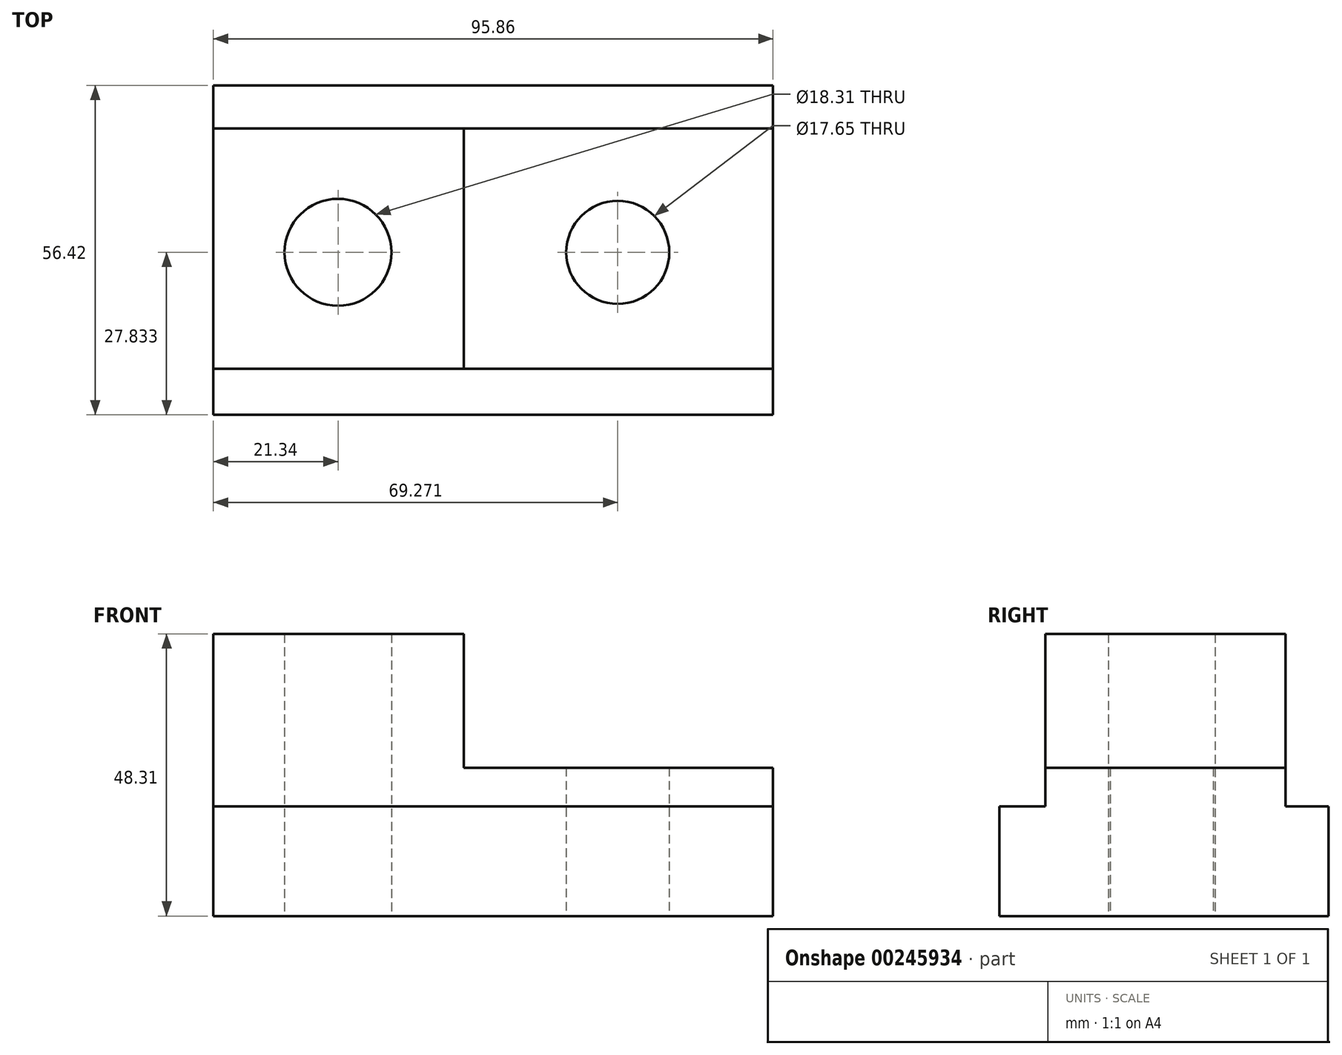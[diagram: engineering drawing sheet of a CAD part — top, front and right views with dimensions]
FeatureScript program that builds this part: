
annotation { "Feature Type Name" : "Feature", "Feature Type Description" : "" }
export const myFeature = defineFeature(function(context is Context, id is Id, definition is map)
    precondition{}
    {
        {
            var Q0;
            Q0=qCreatedBy(makeId("Top.planeOp"),FACE);
            var sketch = newSketch(context, id + "F0", { "sketchPlane" : qUnion([Q0])});
            skLineSegment(sketch, "E0.bottom", {"start": v(-38.7, 19.35) * mm, "end": v(57.17, 19.35) * mm});
            skLineSegment(sketch, "E0.top", {"start": v(-38.7, -37.07) * mm, "end": v(57.17, -37.07) * mm});
            skLineSegment(sketch, "E0.left", {"start": v(-38.7, 19.35) * mm, "end": v(-38.7, -37.07) * mm});
            skLineSegment(sketch, "E0.right", {"start": v(57.17, 19.35) * mm, "end": v(57.17, -37.07) * mm});
            skSolve(sketch);
        }
        {
            var Q0;
            Q0 = qSketchRegion(id + "F0", true);
            extrude(context, id + "F1", {"entities" : qUnion([Q0]), "depth" : 25.4 * mm});
        }
        {
            var Q0;
            Q0=makeQuery(id+"F1.opExtrude","CAP_FACE",FACE,{"disambiguationData":[OSD([sQuery(id+"F0.wireOp",EDGE,"E0.bottom"),sQuery(id+"F0.wireOp",EDGE,"E0.top"),sQuery(id+"F0.wireOp",EDGE,"E0.left"),sQuery(id+"F0.wireOp",EDGE,"E0.right")])],"isStart":false});
            var sketch = newSketch(context, id + "F2", { "sketchPlane" : qUnion([Q0])});
            skLineSegment(sketch, "E1", {"start": v(57.17, -29.2) * mm, "end": v(-38.7, -29.2) * mm});
            skLineSegment(sketch, "E2", {"start": v(-38.7, -29.2) * mm, "end": v(-38.7, -37.07) * mm});
            skLineSegment(sketch, "E3", {"start": v(-38.7, -37.07) * mm, "end": v(57.17, -37.07) * mm});
            skLineSegment(sketch, "E4", {"start": v(57.17, -37.07) * mm, "end": v(57.17, -29.2) * mm});
            skLineSegment(sketch, "E5", {"start": v(57.17, 19.35) * mm, "end": v(-38.7, 19.35) * mm});
            skLineSegment(sketch, "E6", {"start": v(-38.7, 19.35) * mm, "end": v(-38.7, 11.98) * mm});
            skLineSegment(sketch, "E7", {"start": v(-38.7, 11.98) * mm, "end": v(57.17, 11.98) * mm});
            skLineSegment(sketch, "E8", {"start": v(57.17, 11.98) * mm, "end": v(57.17, 19.35) * mm});
            skSolve(sketch);
        }
        {
            var Q0;
            Q0 = qSketchRegion(id + "F2", true);
            extrude(context, id + "F3", {"entities" : qUnion([Q0]), "operationType" : NewBodyOperationType.REMOVE, "oppositeDirection" : true, "depth" : 6.6 * mm});
        }
        {
            var Q0;
            Q0=makeQuery(id+"F1.opExtrude","SWEPT_FACE",FACE,{"disambiguationData":[OSD([sQuery(id+"F0.wireOp",EDGE,"E0.left")])]});
            var sketch = newSketch(context, id + "F4", { "sketchPlane" : qUnion([Q0])});
            skLineSegment(sketch, "E9", {"start": v(29.2, 25.4) * mm, "end": v(29.2, 48.3) * mm});
            skLineSegment(sketch, "E10", {"start": v(29.2, 48.3) * mm, "end": v(-11.98, 48.3) * mm});
            skLineSegment(sketch, "E11", {"start": v(-11.98, 48.3) * mm, "end": v(-11.98, 25.4) * mm});
            skLineSegment(sketch, "E12", {"start": v(-11.98, 25.4) * mm, "end": v(29.2, 25.4) * mm});
            skSolve(sketch);
        }
        {
            var Q0;
            Q0 = qSketchRegion(id + "F4", true);
            extrude(context, id + "F5", {"entities" : qUnion([Q0]), "operationType" : NewBodyOperationType.ADD, "oppositeDirection" : true, "depth" : 42.93 * mm});
        }
        {
            var Q0;
            Q0=qCreatedBy(makeId("Top.planeOp"),FACE);
            var sketch = newSketch(context, id + "F6", { "sketchPlane" : qUnion([Q0])});
            skCircle(sketch, "E13", {"center": v(-17.35, -9.24) * mm, "radius": 9.16 * mm});
            skCircle(sketch, "E14", {"center": v(30.58, -9.24) * mm, "radius": 8.83 * mm});
            skSolve(sketch);
        }
        {
            var Q0;
            Q0 = qSketchRegion(id + "F6", true);
            extrude(context, id + "F7", {"entities" : qUnion([Q0]), "operationType" : NewBodyOperationType.REMOVE, "depth" : 92.96 * mm});
        }
    });
